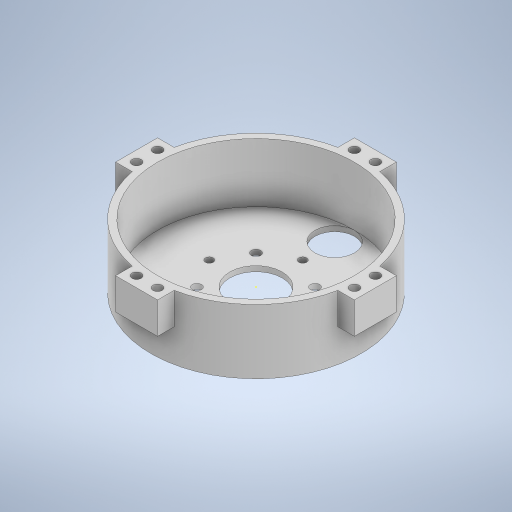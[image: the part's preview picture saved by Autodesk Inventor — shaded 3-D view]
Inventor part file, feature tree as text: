
AUTODESK INVENTOR PART (.ipt)
format: ipt  version: 2023 (Build 270158000, 158)  size: 388,096 bytes
history: native  units: in
note: dims shown in document units (in); Inventor stores cm internally (conversion verified against a paired STEP export)
features: sketch x11, extrude x7, hole x3
ambient origin geometry x8: Origin, YZ Plane, XZ Plane, XY Plane, X Axis, Y Axis, Z Axis, Center Point
bodies: Solid1 (feature_tree)
feature tree (21):
  extrude  "Extrusion1"  Depth=1.375in TaperAngle=0.0deg
  extrude  "Extrusion2"  Depth=1.275in TaperAngle=0.0deg
  extrude  "Extrusion3"  Depth=1.125in TaperAngle=0.0deg
  hole  "Hole1"  [1 undecoded]
  extrude  "Extrusion4"  Depth=0.4in
  extrude  "Extrusion5"  Depth=0.4in
  hole  "Hole2"  [1 undecoded]
  extrude  "Extrusion6"  Depth=0.4in
  hole  "Hole3"  [1 undecoded]
  sketch  "Sketch10"  dims[d28=0.4in d29=0.8in]
  extrude  "Extrusion7"  Depth=0.8in
  sketch  "Sketch1"  dims[d0=4.0in d1=1.375in d2=0.0in]
  sketch  "Sketch2"  dims[d3=3.75in d4=1.275in d5=0.0in]
  sketch  "Sketch3"  dims[d6=1.0in d7=1.125in d8=0.0in]
  sketch  "Sketch4"  dims[d9=1.125in d10=1.125in]
  sketch  "Sketch5"  dims[d11=0.177in d12=0.75in d13=0.332in d14=0.25in d15=0.5635in d16=1.0in d17=0.8108in d18=0.4in]
  sketch  "Sketch6"  dims[d19=0.4in d20=0.4in]
  sketch  "Sketch7"  dims[d21=0.4in d22=0.75in d23=0.0in]
  sketch  "Sketch8"  dims[d24=0.4in d25=0.4in]
  sketch  "Sketch9"  dims[d26=0.8in d27=0.4in]
  sketch  "Sketch11"  dims[d30=0.4in d31=0.4in d32=0.8in d33=0.75in d34=0.0in d35=0.2in d36=0.2in d37=0.4in d38=0.2in d39=0.2in d40=0.4in d41=0.2in d42=0.2in d43=0.2in d44=0.2in d45=0.4in d46=0.177in d47=0.75in d48=0.375in d49=0.25in d50=0.5635in d51=0.75in d52=0.8108in d53=1.5in d54=0.75in d55=0.0in d56=1.259in d57=45.0deg d58=1.259in d59=0.15in d60=0.75in d61=0.279in d62=0.25in d63=0.5635in d64=0.75in d65=0.8108in d66=0.15in d67=0.0in d68=0.5in d69=0.0344in]
note: 3 required parameter values undecoded (feature->parameter linkage not recoverable at this tier; creation-order binding heuristic only, values carry confidence <= 0.55)
